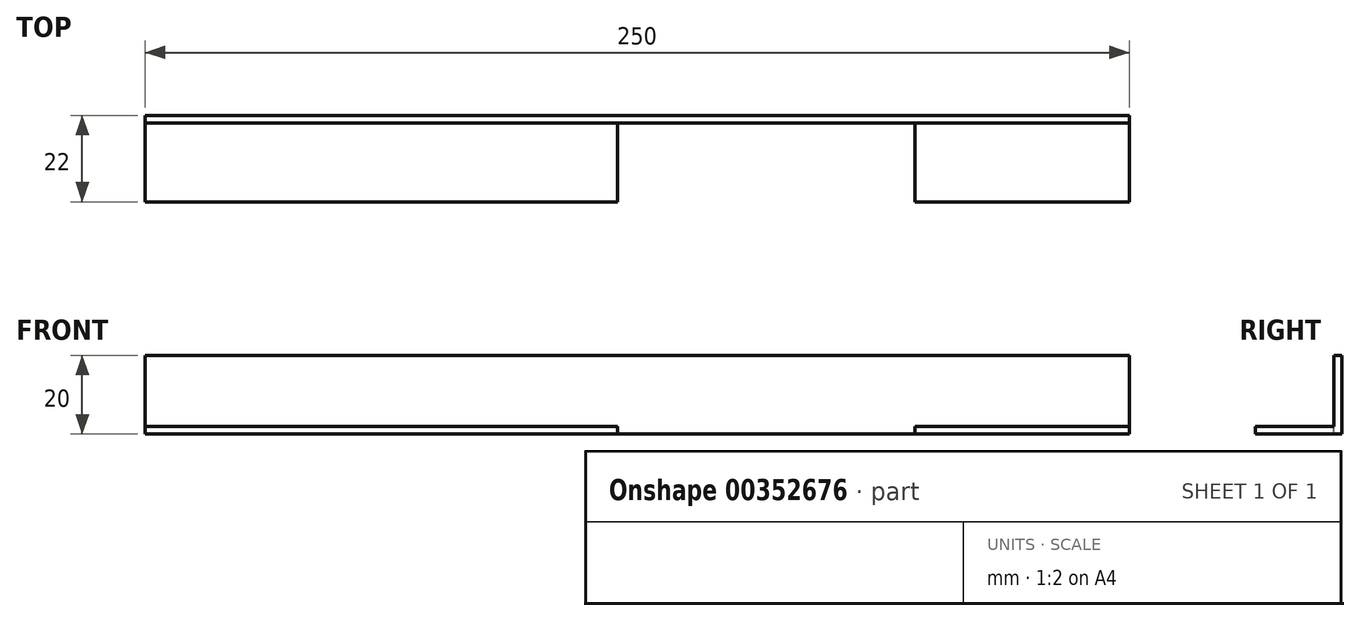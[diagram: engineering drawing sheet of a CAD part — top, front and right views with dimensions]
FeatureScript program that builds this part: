
annotation { "Feature Type Name" : "Feature", "Feature Type Description" : "" }
export const myFeature = defineFeature(function(context is Context, id is Id, definition is map)
    precondition{}
    {
        {
            var Q0;
            Q0=qCreatedBy(makeId("Front.planeOp"),FACE);
            var sketch = newSketch(context, id + "F0", { "sketchPlane" : qUnion([Q0])});
            skLineSegment(sketch, "E0.bottom", {"start": v(0, 0) * mm, "end": v(250, 0) * mm});
            skLineSegment(sketch, "E0.top", {"start": v(0, 20) * mm, "end": v(250, 20) * mm});
            skLineSegment(sketch, "E0.left", {"start": v(0, 0) * mm, "end": v(0, 20) * mm});
            skLineSegment(sketch, "E0.right", {"start": v(250, 0) * mm, "end": v(250, 20) * mm});
            skLineSegment(sketch, "E1.top", {"start": v(0, 2) * mm, "end": v(250, 2) * mm});
            skLineSegment(sketch, "E1.left", {"start": v(0, 0) * mm, "end": v(0, 2) * mm});
            skLineSegment(sketch, "E1.right", {"start": v(250, 0) * mm, "end": v(250, 2) * mm});
            skSolve(sketch);
        }
        {
            var Q0;
            Q0 = qSketchRegion(id + "F0", true);
            extrude(context, id + "F1", {"entities" : qUnion([Q0]), "depth" : 2 * mm});
        }
        {
            var Q0;
            Q0=makeQuery(id+"F0.imprint","IMPRINT",FACE,{"disambiguationData":[TD([[makeQuery(id+"F0.imprint","IMPRINT",EDGE,{"derivedFrom":sQuery(id+"F0.wireOp",EDGE,"E0.bottom")}),1.0]])]});
            extrude(context, id + "F2", {"entities" : qUnion([Q0]), "operationType" : NewBodyOperationType.ADD, "depth" : 22 * mm});
        }
        {
            var Q0;
            Q0=makeQuery(id+"F2.opExtrude","CAP_FACE",FACE,{"disambiguationData":[OSD([sQuery(id+"F0.wireOp",EDGE,"E0.bottom"),sQuery(id+"F0.wireOp",EDGE,"E1.top"),sQuery(id+"F0.wireOp",EDGE,"E1.left"),sQuery(id+"F0.wireOp",EDGE,"E1.right")])],"isStart":false});
            var sketch = newSketch(context, id + "F3", { "sketchPlane" : qUnion([Q0])});
            skLineSegment(sketch, "E2.bottom", {"start": v(120, 2) * mm, "end": v(195.5, 2) * mm});
            skLineSegment(sketch, "E2.top", {"start": v(120, 0) * mm, "end": v(195.5, 0) * mm});
            skLineSegment(sketch, "E2.left", {"start": v(120, 2) * mm, "end": v(120, 0) * mm});
            skLineSegment(sketch, "E2.right", {"start": v(195.5, 2) * mm, "end": v(195.5, 0) * mm});
            skSolve(sketch);
        }
        {
            var Q0;
            Q0 = qSketchRegion(id + "F3", true);
            var Q1;
            Q1=makeQuery(id+"F1.opExtrude","CAP_FACE",FACE,{"disambiguationData":[OSD([sQuery(id+"F0.wireOp",EDGE,"E0.top"),sQuery(id+"F0.wireOp",EDGE,"E0.left"),sQuery(id+"F0.wireOp",EDGE,"E0.right"),sQuery(id+"F0.wireOp",EDGE,"E0.bottom"),sQuery(id+"F0.wireOp",EDGE,"E1.left"),sQuery(id+"F0.wireOp",EDGE,"E1.right")])],"isStart":false});
            extrude(context, id + "F4", {"entities" : qUnion([Q0]), "operationType" : NewBodyOperationType.REMOVE, "endBound" : BoundingType.UP_TO_SURFACE, "oppositeDirection" : true, "endBoundEntityFace" : qUnion([Q1]), "depth" : 20 * mm});
        }
    });
